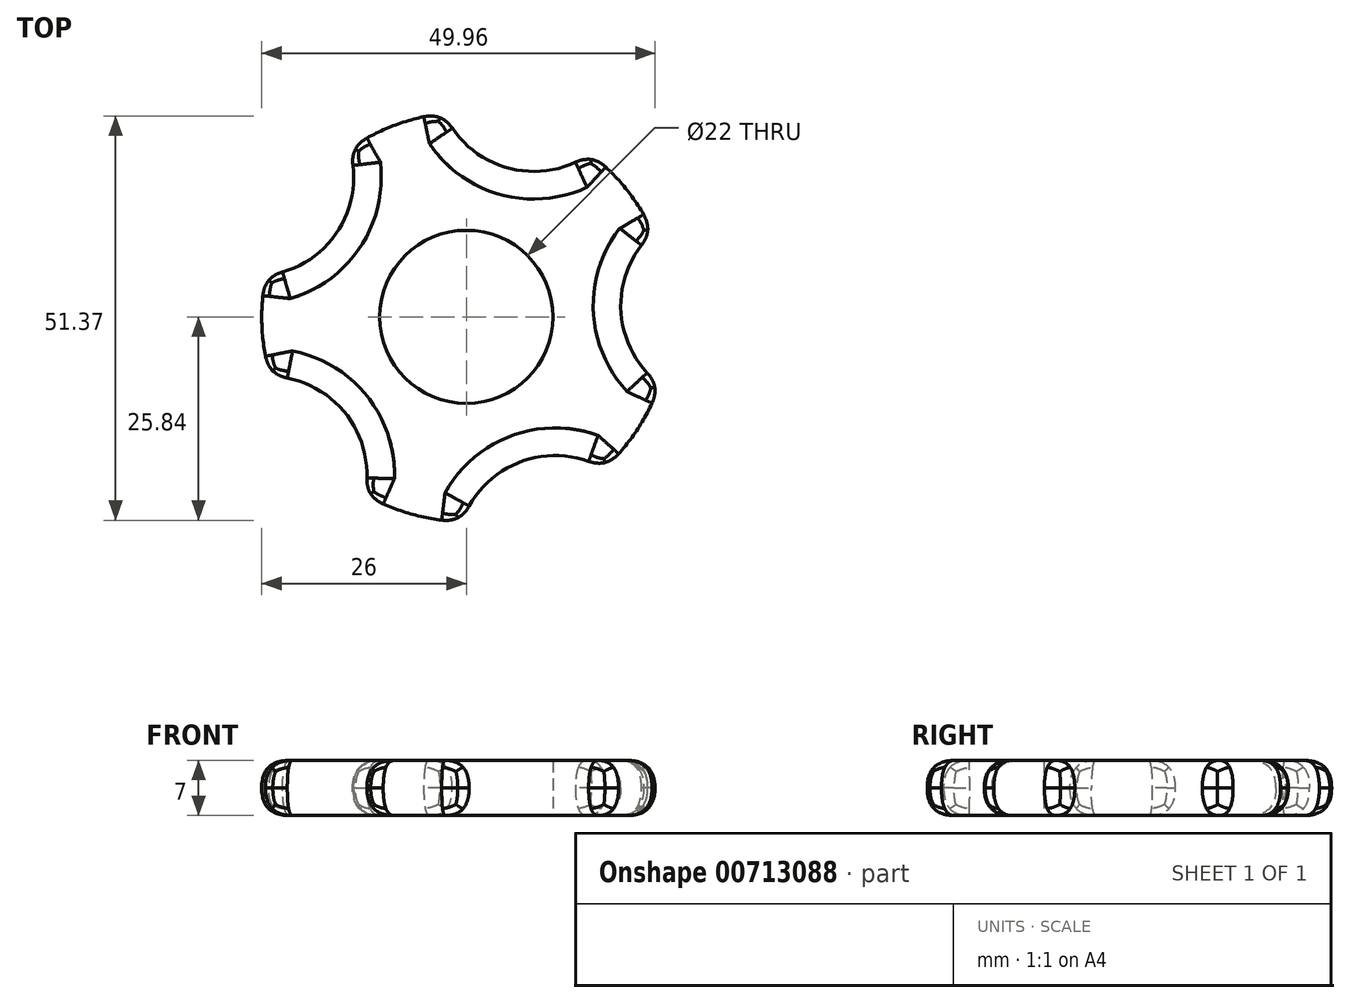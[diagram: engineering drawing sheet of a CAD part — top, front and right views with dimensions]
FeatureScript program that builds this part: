
annotation { "Feature Type Name" : "Feature", "Feature Type Description" : "" }
export const myFeature = defineFeature(function(context is Context, id is Id, definition is map)
    precondition{}
    {
        {
            var Q0;
            Q0=qCreatedBy(makeId("Top.planeOp"),FACE);
            var sketch = newSketch(context, id + "F0", { "sketchPlane" : qUnion([Q0])});
            skCircle(sketch, "E0", {"center": v(0, 0) * mm, "radius": 26 * mm});
            skCircle(sketch, "E1.cCircle", {"center": v(0, 0) * mm, "radius": 26 * mm, "construction": true});
            skLineSegment(sketch, "E1.0", {"start": v(32.1, 1.43) * mm, "end": v(11.28, -30.1) * mm});
            skLineSegment(sketch, "E1.1", {"start": v(11.28, -30.1) * mm, "end": v(-25.13, -20.03) * mm});
            skLineSegment(sketch, "E1.2", {"start": v(-25.13, -20.03) * mm, "end": v(-26.81, 17.71) * mm});
            skLineSegment(sketch, "E1.3", {"start": v(-26.81, 17.71) * mm, "end": v(8.56, 30.98) * mm});
            skLineSegment(sketch, "E1.4", {"start": v(8.56, 30.98) * mm, "end": v(32.1, 1.43) * mm});
            skPoint(sketch, "E1.0.midPoint", {"position": v(21.7, -14.33) * mm});
            skCircle(sketch, "E2", {"center": v(0, 0) * mm, "radius": 11 * mm});
            skCircle(sketch, "E3", {"center": v(11.28, -30.1) * mm, "radius": 12.5 * mm});
            skCircle(sketch, "E4", {"center": v(-25.13, -20.03) * mm, "radius": 12.5 * mm});
            skCircle(sketch, "E5", {"center": v(-26.81, 17.71) * mm, "radius": 12.5 * mm});
            skCircle(sketch, "E6", {"center": v(8.56, 30.98) * mm, "radius": 12.5 * mm});
            skCircle(sketch, "E7", {"center": v(32.1, 1.43) * mm, "radius": 12.5 * mm});
            skSolve(sketch);
        }
        {
            var Q0;
            Q0=makeQuery(id+"F0.imprint","IMPRINT",FACE,{"disambiguationData":[TD([[makeQuery(id+"F0.imprint","IMPRINT",EDGE,{"derivedFrom":sQuery(id+"F0.wireOp",EDGE,"E2")}),-1.0]])]});
            extrude(context, id + "F1", {"entities" : qUnion([Q0]), "depth" : 7 * mm, "offsetDistance" : 25 * mm});
        }
        {
            var Q0;
            Q0=makeQuery(id+"F1.opExtrude","CAP_EDGE",EDGE,{"disambiguationData":[OSD([sQuery(id+"F0.wireOp",EDGE,"E5")])],"isStart":false});
            var Q1;
            {var subQ0=sQuery(id+"F0.wireOp",EDGE,"E0");var subQ1=makeQuery(id+"F0.imprint","INTERSECT",VERTEX,{"derivedFrom":[subQ0,sQuery(id+"F0.wireOp",EDGE,"E1.3")]});Q1=makeQuery(id+"F1.opExtrude","CAP_EDGE",EDGE,{"disambiguationData":[OSD([subQ0]),TDD([makeQuery(id+"F0.imprint","IMPRINT",EDGE,{"disambiguationData":[TD([[subQ1,1.0]])],"derivedFrom":subQ0}),makeQuery(id+"F0.imprint","IMPRINT",EDGE,{"disambiguationData":[TD([[subQ1,-1.0]])],"derivedFrom":subQ0})])],"isStart":false});}
            var Q2;
            {var subQ0=sQuery(id+"F0.wireOp",EDGE,"E0");var subQ1=makeQuery(id+"F0.imprint","INTERSECT",VERTEX,{"derivedFrom":[subQ0,sQuery(id+"F0.wireOp",EDGE,"E1.2")]});Q2=makeQuery(id+"F1.opExtrude","CAP_EDGE",EDGE,{"disambiguationData":[OSD([subQ0]),TDD([makeQuery(id+"F0.imprint","IMPRINT",EDGE,{"disambiguationData":[TD([[subQ1,1.0]])],"derivedFrom":subQ0}),makeQuery(id+"F0.imprint","IMPRINT",EDGE,{"disambiguationData":[TD([[subQ1,-1.0]])],"derivedFrom":subQ0})])],"isStart":false});}
            var Q3;
            Q3=makeQuery(id+"F1.opExtrude","CAP_EDGE",EDGE,{"disambiguationData":[OSD([sQuery(id+"F0.wireOp",EDGE,"E4")])],"isStart":false});
            var Q4;
            {var subQ0=sQuery(id+"F0.wireOp",EDGE,"E0");var subQ1=makeQuery(id+"F0.imprint","INTERSECT",VERTEX,{"derivedFrom":[subQ0,sQuery(id+"F0.wireOp",EDGE,"E1.1")]});Q4=makeQuery(id+"F1.opExtrude","CAP_EDGE",EDGE,{"disambiguationData":[OSD([subQ0]),TDD([makeQuery(id+"F0.imprint","IMPRINT",EDGE,{"disambiguationData":[TD([[subQ1,1.0]])],"derivedFrom":subQ0}),makeQuery(id+"F0.imprint","IMPRINT",EDGE,{"disambiguationData":[TD([[subQ1,-1.0]])],"derivedFrom":subQ0})])],"isStart":false});}
            var Q5;
            Q5=makeQuery(id+"F1.opExtrude","CAP_EDGE",EDGE,{"disambiguationData":[OSD([sQuery(id+"F0.wireOp",EDGE,"E3")])],"isStart":false});
            var Q6;
            {var subQ0=sQuery(id+"F0.wireOp",EDGE,"E0");var subQ1=makeQuery(id+"F0.imprint","INTERSECT",VERTEX,{"derivedFrom":[subQ0,sQuery(id+"F0.wireOp",EDGE,"E1.0")]});Q6=makeQuery(id+"F1.opExtrude","CAP_EDGE",EDGE,{"disambiguationData":[OSD([subQ0]),TDD([makeQuery(id+"F0.imprint","IMPRINT",EDGE,{"disambiguationData":[TD([[subQ1,1.0]])],"derivedFrom":subQ0}),makeQuery(id+"F0.imprint","IMPRINT",EDGE,{"disambiguationData":[TD([[subQ1,-1.0]])],"derivedFrom":subQ0})])],"isStart":true});}
            var Q7;
            Q7=makeQuery(id+"F1.opExtrude","CAP_EDGE",EDGE,{"disambiguationData":[OSD([sQuery(id+"F0.wireOp",EDGE,"E7")])],"isStart":true});
            var Q8;
            {var subQ0=sQuery(id+"F0.wireOp",EDGE,"E0");var subQ1=makeQuery(id+"F0.imprint","INTERSECT",VERTEX,{"derivedFrom":[subQ0,sQuery(id+"F0.wireOp",EDGE,"E1.4")]});Q8=makeQuery(id+"F1.opExtrude","CAP_EDGE",EDGE,{"disambiguationData":[OSD([subQ0]),TDD([makeQuery(id+"F0.imprint","IMPRINT",EDGE,{"disambiguationData":[TD([[subQ1,1.0]])],"derivedFrom":subQ0}),makeQuery(id+"F0.imprint","IMPRINT",EDGE,{"disambiguationData":[TD([[subQ1,-1.0]])],"derivedFrom":subQ0})])],"isStart":false});}
            var Q9;
            Q9=makeQuery(id+"F1.opExtrude","CAP_EDGE",EDGE,{"disambiguationData":[OSD([sQuery(id+"F0.wireOp",EDGE,"E6")])],"isStart":false});
            var Q10;
            {var subQ0=sQuery(id+"F0.wireOp",EDGE,"E0");var subQ1=makeQuery(id+"F0.imprint","INTERSECT",VERTEX,{"derivedFrom":[subQ0,sQuery(id+"F0.wireOp",EDGE,"E1.3")]});Q10=makeQuery(id+"F1.opExtrude","CAP_EDGE",EDGE,{"disambiguationData":[OSD([subQ0]),TDD([makeQuery(id+"F0.imprint","IMPRINT",EDGE,{"disambiguationData":[TD([[subQ1,1.0]])],"derivedFrom":subQ0}),makeQuery(id+"F0.imprint","IMPRINT",EDGE,{"disambiguationData":[TD([[subQ1,-1.0]])],"derivedFrom":subQ0})])],"isStart":true});}
            var Q11;
            Q11=makeQuery(id+"F1.opExtrude","CAP_EDGE",EDGE,{"disambiguationData":[OSD([sQuery(id+"F0.wireOp",EDGE,"E6")])],"isStart":true});
            var Q12;
            {var subQ0=sQuery(id+"F0.wireOp",EDGE,"E0");var subQ1=makeQuery(id+"F0.imprint","INTERSECT",VERTEX,{"derivedFrom":[subQ0,sQuery(id+"F0.wireOp",EDGE,"E1.4")]});Q12=makeQuery(id+"F1.opExtrude","CAP_EDGE",EDGE,{"disambiguationData":[OSD([subQ0]),TDD([makeQuery(id+"F0.imprint","IMPRINT",EDGE,{"disambiguationData":[TD([[subQ1,1.0]])],"derivedFrom":subQ0}),makeQuery(id+"F0.imprint","IMPRINT",EDGE,{"disambiguationData":[TD([[subQ1,-1.0]])],"derivedFrom":subQ0})])],"isStart":true});}
            var Q13;
            Q13=makeQuery(id+"F1.opExtrude","CAP_EDGE",EDGE,{"disambiguationData":[OSD([sQuery(id+"F0.wireOp",EDGE,"E5")])],"isStart":true});
            var Q14;
            {var subQ0=sQuery(id+"F0.wireOp",EDGE,"E0");var subQ1=makeQuery(id+"F0.imprint","INTERSECT",VERTEX,{"derivedFrom":[subQ0,sQuery(id+"F0.wireOp",EDGE,"E1.2")]});Q14=makeQuery(id+"F1.opExtrude","CAP_EDGE",EDGE,{"disambiguationData":[OSD([subQ0]),TDD([makeQuery(id+"F0.imprint","IMPRINT",EDGE,{"disambiguationData":[TD([[subQ1,1.0]])],"derivedFrom":subQ0}),makeQuery(id+"F0.imprint","IMPRINT",EDGE,{"disambiguationData":[TD([[subQ1,-1.0]])],"derivedFrom":subQ0})])],"isStart":true});}
            var Q15;
            {var subQ0=sQuery(id+"F0.wireOp",EDGE,"E5");var subQ1=sQuery(id+"F0.wireOp",EDGE,"E0");Q15=makeQuery(id+"F1.opExtrude","SWEPT_EDGE",EDGE,{"disambiguationData":[OSD([subQ1,subQ0]),TDD([makeQuery(id+"F0.imprint","INTERSECT",VERTEX,{"disambiguationData":[OD(1.0)],"derivedFrom":[subQ1,subQ0]})])]});}
            var Q16;
            Q16=makeQuery(id+"F1.opExtrude","CAP_EDGE",EDGE,{"disambiguationData":[OSD([sQuery(id+"F0.wireOp",EDGE,"E4")])],"isStart":true});
            var Q17;
            {var subQ0=sQuery(id+"F0.wireOp",EDGE,"E4");var subQ1=sQuery(id+"F0.wireOp",EDGE,"E0");Q17=makeQuery(id+"F1.opExtrude","SWEPT_EDGE",EDGE,{"disambiguationData":[OSD([subQ1,subQ0]),TDD([makeQuery(id+"F0.imprint","INTERSECT",VERTEX,{"disambiguationData":[OD(0.0)],"derivedFrom":[subQ1,subQ0]})])]});}
            var Q18;
            {var subQ0=sQuery(id+"F0.wireOp",EDGE,"E4");var subQ1=sQuery(id+"F0.wireOp",EDGE,"E0");Q18=makeQuery(id+"F1.opExtrude","SWEPT_EDGE",EDGE,{"disambiguationData":[OSD([subQ1,subQ0]),TDD([makeQuery(id+"F0.imprint","INTERSECT",VERTEX,{"disambiguationData":[OD(1.0)],"derivedFrom":[subQ1,subQ0]})])]});}
            var Q19;
            {var subQ0=sQuery(id+"F0.wireOp",EDGE,"E0");var subQ1=makeQuery(id+"F0.imprint","INTERSECT",VERTEX,{"derivedFrom":[subQ0,sQuery(id+"F0.wireOp",EDGE,"E1.1")]});Q19=makeQuery(id+"F1.opExtrude","CAP_EDGE",EDGE,{"disambiguationData":[OSD([subQ0]),TDD([makeQuery(id+"F0.imprint","IMPRINT",EDGE,{"disambiguationData":[TD([[subQ1,1.0]])],"derivedFrom":subQ0}),makeQuery(id+"F0.imprint","IMPRINT",EDGE,{"disambiguationData":[TD([[subQ1,-1.0]])],"derivedFrom":subQ0})])],"isStart":true});}
            var Q20;
            {var subQ0=sQuery(id+"F0.wireOp",EDGE,"E3");var subQ1=sQuery(id+"F0.wireOp",EDGE,"E0");Q20=makeQuery(id+"F1.opExtrude","SWEPT_EDGE",EDGE,{"disambiguationData":[OSD([subQ1,subQ0]),TDD([makeQuery(id+"F0.imprint","INTERSECT",VERTEX,{"disambiguationData":[OD(0.0)],"derivedFrom":[subQ1,subQ0]})])]});}
            var Q21;
            Q21=makeQuery(id+"F1.opExtrude","CAP_EDGE",EDGE,{"disambiguationData":[OSD([sQuery(id+"F0.wireOp",EDGE,"E3")])],"isStart":true});
            var Q22;
            {var subQ0=sQuery(id+"F0.wireOp",EDGE,"E3");var subQ1=sQuery(id+"F0.wireOp",EDGE,"E0");Q22=makeQuery(id+"F1.opExtrude","SWEPT_EDGE",EDGE,{"disambiguationData":[OSD([subQ1,subQ0]),TDD([makeQuery(id+"F0.imprint","INTERSECT",VERTEX,{"disambiguationData":[OD(1.0)],"derivedFrom":[subQ1,subQ0]})])]});}
            var Q23;
            {var subQ0=sQuery(id+"F0.wireOp",EDGE,"E0");var subQ1=makeQuery(id+"F0.imprint","INTERSECT",VERTEX,{"derivedFrom":[subQ0,sQuery(id+"F0.wireOp",EDGE,"E1.0")]});Q23=makeQuery(id+"F1.opExtrude","CAP_EDGE",EDGE,{"disambiguationData":[OSD([subQ0]),TDD([makeQuery(id+"F0.imprint","IMPRINT",EDGE,{"disambiguationData":[TD([[subQ1,1.0]])],"derivedFrom":subQ0}),makeQuery(id+"F0.imprint","IMPRINT",EDGE,{"disambiguationData":[TD([[subQ1,-1.0]])],"derivedFrom":subQ0})])],"isStart":false});}
            var Q24;
            {var subQ0=sQuery(id+"F0.wireOp",EDGE,"E7");var subQ1=sQuery(id+"F0.wireOp",EDGE,"E0");Q24=makeQuery(id+"F1.opExtrude","SWEPT_EDGE",EDGE,{"disambiguationData":[OSD([subQ1,subQ0]),TDD([makeQuery(id+"F0.imprint","INTERSECT",VERTEX,{"disambiguationData":[OD(1.0)],"derivedFrom":[subQ1,subQ0]})])]});}
            var Q25;
            Q25=makeQuery(id+"F1.opExtrude","CAP_EDGE",EDGE,{"disambiguationData":[OSD([sQuery(id+"F0.wireOp",EDGE,"E7")])],"isStart":false});
            var Q26;
            {var subQ0=sQuery(id+"F0.wireOp",EDGE,"E7");var subQ1=sQuery(id+"F0.wireOp",EDGE,"E0");Q26=makeQuery(id+"F1.opExtrude","SWEPT_EDGE",EDGE,{"disambiguationData":[OSD([subQ1,subQ0]),TDD([makeQuery(id+"F0.imprint","INTERSECT",VERTEX,{"disambiguationData":[OD(0.0)],"derivedFrom":[subQ1,subQ0]})])]});}
            var Q27;
            {var subQ0=sQuery(id+"F0.wireOp",EDGE,"E5");var subQ1=sQuery(id+"F0.wireOp",EDGE,"E0");Q27=makeQuery(id+"F1.opExtrude","SWEPT_EDGE",EDGE,{"disambiguationData":[OSD([subQ1,subQ0]),TDD([makeQuery(id+"F0.imprint","INTERSECT",VERTEX,{"disambiguationData":[OD(0.0)],"derivedFrom":[subQ1,subQ0]})])]});}
            var Q28;
            {var subQ0=sQuery(id+"F0.wireOp",EDGE,"E6");var subQ1=sQuery(id+"F0.wireOp",EDGE,"E0");Q28=makeQuery(id+"F1.opExtrude","SWEPT_EDGE",EDGE,{"disambiguationData":[OSD([subQ1,subQ0]),TDD([makeQuery(id+"F0.imprint","INTERSECT",VERTEX,{"disambiguationData":[OD(1.0)],"derivedFrom":[subQ1,subQ0]})])]});}
            var Q29;
            {var subQ0=sQuery(id+"F0.wireOp",EDGE,"E6");var subQ1=sQuery(id+"F0.wireOp",EDGE,"E0");Q29=makeQuery(id+"F1.opExtrude","SWEPT_EDGE",EDGE,{"disambiguationData":[OSD([subQ1,subQ0]),TDD([makeQuery(id+"F0.imprint","INTERSECT",VERTEX,{"disambiguationData":[OD(0.0)],"derivedFrom":[subQ1,subQ0]})])]});}
            fillet(context, id + "F2", {"entities" : qUnion([Q0, Q1, Q2, Q3, Q4, Q5, Q6, Q7, Q8, Q9, Q10, Q11, Q12, Q13, Q14, Q15, Q16, Q17, Q18, Q19, Q20, Q21, Q22, Q23, Q24, Q25, Q26, Q27, Q28, Q29]), "radius" : 3.5 * mm, "tangentPropagation" : true, "rho" : 0.5, "crossSection" : FilletCrossSection.CONIC, "allowEdgeOverflow" : false});
        }
    });
